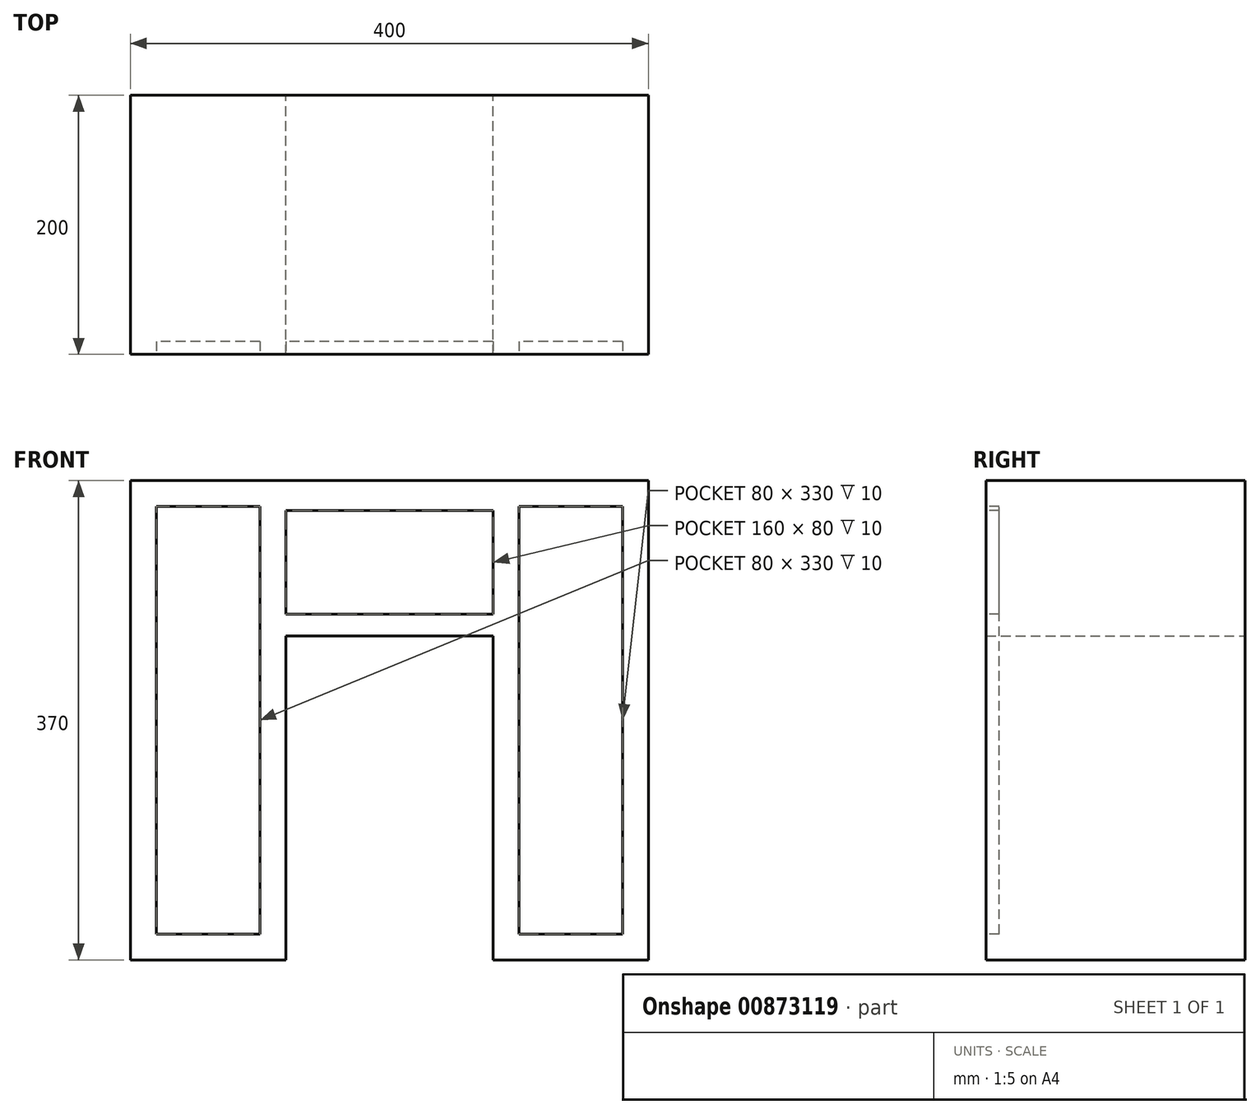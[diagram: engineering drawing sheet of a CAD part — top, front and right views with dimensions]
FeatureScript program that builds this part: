
annotation { "Feature Type Name" : "Feature", "Feature Type Description" : "" }
export const myFeature = defineFeature(function(context is Context, id is Id, definition is map)
    precondition{}
    {
        {
            var Q0;
            Q0=qCreatedBy(makeId("Front.planeOp"),FACE);
            var sketch = newSketch(context, id + "F0", { "sketchPlane" : qUnion([Q0])});
            skLineSegment(sketch, "E0.bottom", {"start": v(200, -185) * mm, "end": v(80, -185) * mm});
            skLineSegment(sketch, "E0.top", {"start": v(200, 185) * mm, "end": v(-200, 185) * mm});
            skLineSegment(sketch, "E0.left", {"start": v(200, -185) * mm, "end": v(200, 185) * mm});
            skLineSegment(sketch, "E0.right", {"start": v(-200, -185) * mm, "end": v(-200, 185) * mm});
            skPoint(sketch, "E0.middle", {"position": v(0, 0) * mm});
            skLineSegment(sketch, "E1", {"start": v(-200, -185) * mm, "end": v(-80, -185) * mm});
            skPoint(sketch, "E2.end.orphan", {"position": v(-80, 65) * mm});
            skLineSegment(sketch, "E3", {"start": v(-80, -185) * mm, "end": v(-80, 65) * mm});
            skLineSegment(sketch, "E4", {"start": v(-80, 65) * mm, "end": v(80, 65) * mm});
            skLineSegment(sketch, "E5", {"start": v(80, 65) * mm, "end": v(80, -185) * mm});
            skLineSegment(sketch, "E6", {"start": v(80, -185) * mm, "end": v(71.65, -185.58) * mm});
            skLineSegment(sketch, "E7.trimOffspring", {"start": v(-80, -185) * mm, "end": v(-200, -185) * mm});
            skSolve(sketch);
        }
        {
            var Q0;
            Q0 = qSketchRegion(id + "F0", true);
            extrude(context, id + "F1", {"entities" : qUnion([Q0]), "depth" : 200 * mm, "offsetDistance" : 25 * mm});
        }
        {
            var Q0;
            Q0=makeQuery(id+"F1.opExtrude","CAP_FACE",FACE,{"disambiguationData":[OSD([sQuery(id+"F0.wireOp",EDGE,"E0.bottom"),sQuery(id+"F0.wireOp",EDGE,"E0.top"),sQuery(id+"F0.wireOp",EDGE,"E0.left"),sQuery(id+"F0.wireOp",EDGE,"E0.right"),sQuery(id+"F0.wireOp",EDGE,"E3"),sQuery(id+"F0.wireOp",EDGE,"E4"),sQuery(id+"F0.wireOp",EDGE,"E5"),sQuery(id+"F0.wireOp",EDGE,"E7.trimOffspring")])],"isStart":false});
            var sketch = newSketch(context, id + "F2", { "sketchPlane" : qUnion([Q0])});
            skLineSegment(sketch, "E8.bottom", {"start": v(-100, -165) * mm, "end": v(-180, -165) * mm});
            skLineSegment(sketch, "E8.top", {"start": v(-100, 165) * mm, "end": v(-180, 165) * mm});
            skLineSegment(sketch, "E8.left", {"start": v(-100, -165) * mm, "end": v(-100, 165) * mm});
            skLineSegment(sketch, "E8.right", {"start": v(-180, -165) * mm, "end": v(-180, 165) * mm});
            skPoint(sketch, "E8.middle", {"position": v(-140, 0) * mm});
            skPoint(sketch, "E8.middle.positionSnap0", {"position": v(-200, 0) * mm});
            skPoint(sketch, "E8.middle.positionSnap1", {"position": v(-140, -185) * mm});
            skPoint(sketch, "E8.centerSnap0", {"position": v(-200, 0) * mm});
            skPoint(sketch, "E8.centerSnap1", {"position": v(-140, -185) * mm});
            skLineSegment(sketch, "E9.bottom", {"start": v(180, -165) * mm, "end": v(100, -165) * mm});
            skLineSegment(sketch, "E9.top", {"start": v(180, 165) * mm, "end": v(100, 165) * mm});
            skLineSegment(sketch, "E9.left", {"start": v(180, -165) * mm, "end": v(180, 165) * mm});
            skLineSegment(sketch, "E9.right", {"start": v(100, -165) * mm, "end": v(100, 165) * mm});
            skPoint(sketch, "E9.middle", {"position": v(140, 0) * mm});
            skPoint(sketch, "E9.middle.positionSnap0", {"position": v(140, -185) * mm});
            skPoint(sketch, "E9.centerSnap0", {"position": v(140, -185) * mm});
            skLineSegment(sketch, "E10.bottom", {"start": v(80, 81.95) * mm, "end": v(-80, 81.95) * mm});
            skLineSegment(sketch, "E10.top", {"start": v(80, 161.95) * mm, "end": v(-80, 161.95) * mm});
            skLineSegment(sketch, "E10.left", {"start": v(80, 81.95) * mm, "end": v(80, 161.95) * mm});
            skLineSegment(sketch, "E10.right", {"start": v(-80, 81.95) * mm, "end": v(-80, 161.95) * mm});
            skPoint(sketch, "E10.middle", {"position": v(0, 121.95) * mm});
            skPoint(sketch, "E10.middle.positionSnap0", {"position": v(0, 185) * mm});
            skPoint(sketch, "E10.centerSnap0", {"position": v(0, 185) * mm});
            skSolve(sketch);
        }
        {
            var Q0;
            Q0=makeQuery(id+"F2.imprint","IMPRINT",FACE,{"disambiguationData":[TD([[makeQuery(id+"F2.imprint","IMPRINT",EDGE,{"derivedFrom":sQuery(id+"F2.wireOp",EDGE,"E8.bottom")}),-1.0]])]});
            var Q1;
            Q1=makeQuery(id+"F2.imprint","IMPRINT",FACE,{"disambiguationData":[TD([[makeQuery(id+"F2.imprint","IMPRINT",EDGE,{"derivedFrom":sQuery(id+"F2.wireOp",EDGE,"E10.bottom")}),-1.0]])]});
            var Q2;
            Q2=makeQuery(id+"F2.imprint","IMPRINT",FACE,{"disambiguationData":[TD([[makeQuery(id+"F2.imprint","IMPRINT",EDGE,{"derivedFrom":sQuery(id+"F2.wireOp",EDGE,"E9.bottom")}),-1.0]])]});
            extrude(context, id + "F3", {"entities" : qUnion([Q0, Q1, Q2]), "operationType" : NewBodyOperationType.REMOVE, "oppositeDirection" : true, "depth" : 10 * mm, "offsetDistance" : 25 * mm});
        }
    });
